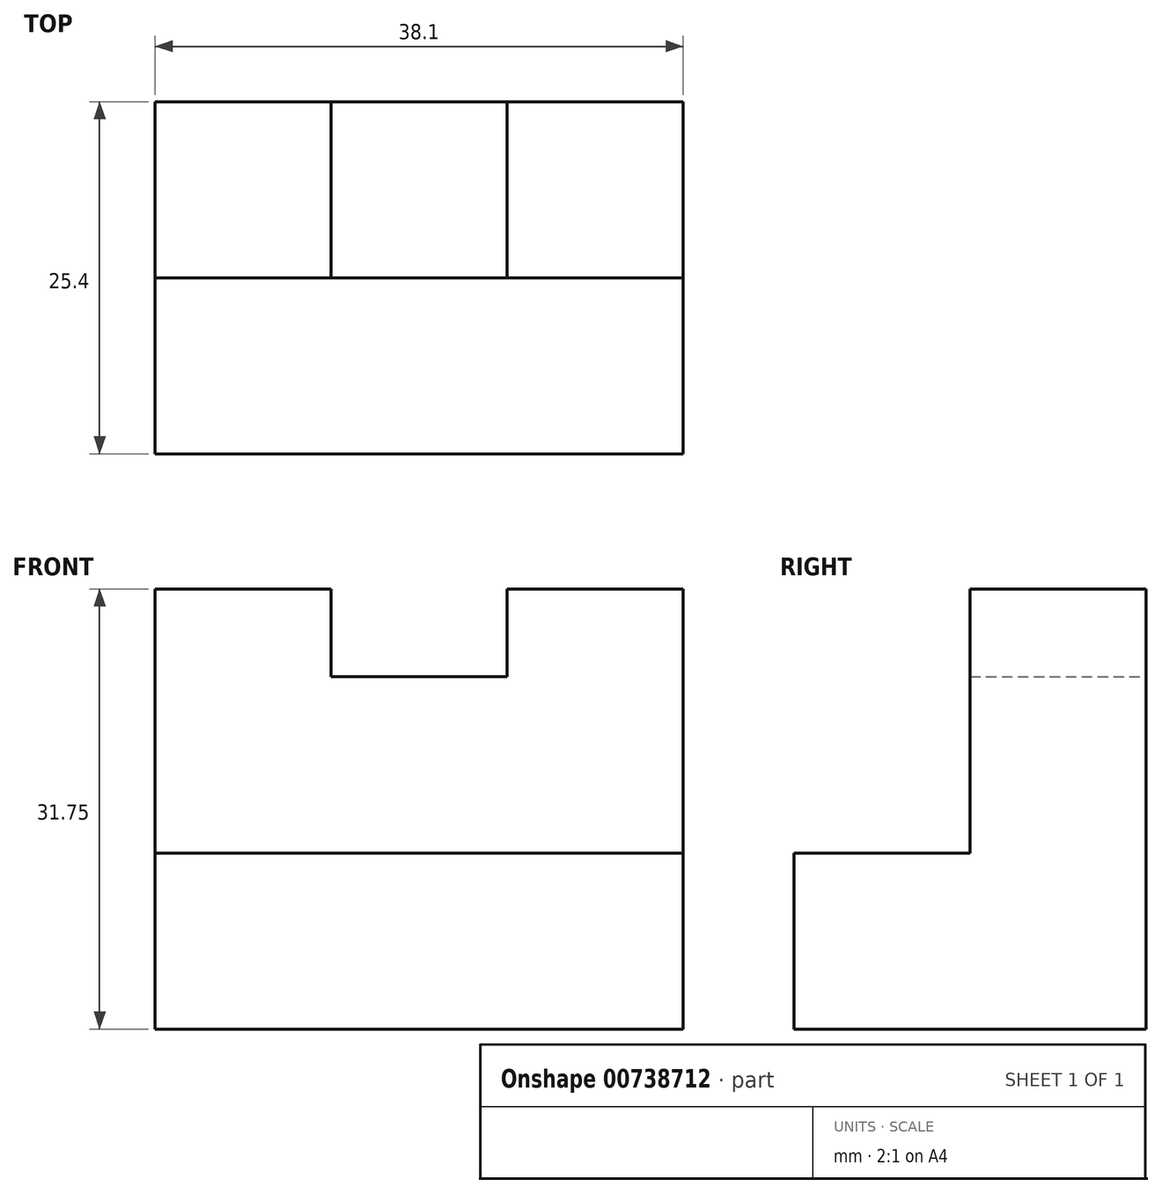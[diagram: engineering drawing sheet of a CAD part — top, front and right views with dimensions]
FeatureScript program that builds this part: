
annotation { "Feature Type Name" : "Feature", "Feature Type Description" : "" }
export const myFeature = defineFeature(function(context is Context, id is Id, definition is map)
    precondition{}
    {
        {
            var Q0;
            Q0=qCreatedBy(makeId("Right.planeOp"),FACE);
            var sketch = newSketch(context, id + "F0", { "sketchPlane" : qUnion([Q0])});
            skLineSegment(sketch, "E0", {"start": v(0, 31.75) * mm, "end": v(0, 0) * mm});
            skLineSegment(sketch, "E1", {"start": v(0, 0) * mm, "end": v(-25.4, 0) * mm});
            skLineSegment(sketch, "E2", {"start": v(-25.4, 0) * mm, "end": v(-25.4, 12.7) * mm});
            skLineSegment(sketch, "E3", {"start": v(-25.4, 12.7) * mm, "end": v(-12.7, 12.7) * mm});
            skLineSegment(sketch, "E4", {"start": v(-12.7, 12.7) * mm, "end": v(-12.7, 31.75) * mm});
            skLineSegment(sketch, "E5", {"start": v(-12.7, 31.75) * mm, "end": v(0, 31.75) * mm});
            skSolve(sketch);
        }
        {
            var Q0;
            Q0 = qSketchRegion(id + "F0", true);
            extrude(context, id + "F1", {"entities" : qUnion([Q0]), "depth" : 38.1 * mm, "offsetDistance" : 25.4 * mm});
        }
        {
            var Q0;
            Q0=qCreatedBy(makeId("Front.planeOp"),FACE);
            var sketch = newSketch(context, id + "F2", { "sketchPlane" : qUnion([Q0])});
            skLineSegment(sketch, "E6", {"start": v(12.7, 32.22) * mm, "end": v(12.7, 25.87) * mm});
            skLineSegment(sketch, "E7", {"start": v(12.7, 25.87) * mm, "end": v(25.4, 25.87) * mm});
            skLineSegment(sketch, "E8", {"start": v(25.4, 25.87) * mm, "end": v(25.4, 32.22) * mm});
            skLineSegment(sketch, "E9", {"start": v(25.4, 32.22) * mm, "end": v(12.7, 32.22) * mm});
            skSolve(sketch);
        }
        {
            var Q0;
            Q0 = qSketchRegion(id + "F2", true);
            extrude(context, id + "F3", {"entities" : qUnion([Q0]), "operationType" : NewBodyOperationType.REMOVE, "endBound" : BoundingType.THROUGH_ALL, "oppositeDirection" : true, "depth" : 25.4 * mm, "offsetDistance" : 25.4 * mm});
        }
        {
            var Q0;
            Q0=qCreatedBy(makeId("Front.planeOp"),FACE);
            var sketch = newSketch(context, id + "F4", { "sketchPlane" : qUnion([Q0])});
            skLineSegment(sketch, "E10", {"start": v(12.7, 31.77) * mm, "end": v(12.7, 25.42) * mm});
            skLineSegment(sketch, "E11", {"start": v(12.7, 25.42) * mm, "end": v(25.4, 25.42) * mm});
            skLineSegment(sketch, "E12", {"start": v(25.4, 25.42) * mm, "end": v(25.4, 31.77) * mm});
            skLineSegment(sketch, "E13", {"start": v(25.4, 31.77) * mm, "end": v(12.7, 31.77) * mm});
            skSolve(sketch);
        }
        {
            var Q0;
            Q0 = qSketchRegion(id + "F4", true);
            extrude(context, id + "F5", {"entities" : qUnion([Q0]), "operationType" : NewBodyOperationType.REMOVE, "endBound" : BoundingType.THROUGH_ALL, "oppositeDirection" : true, "depth" : 25.4 * mm, "offsetDistance" : 25.4 * mm});
        }
        {
            var Q0;
            Q0=qCreatedBy(makeId("Front.planeOp"),FACE);
            var sketch = newSketch(context, id + "F6", { "sketchPlane" : qUnion([Q0])});
            skLineSegment(sketch, "E14", {"start": v(12.7, 32.14) * mm, "end": v(12.7, 25.79) * mm});
            skLineSegment(sketch, "E15", {"start": v(12.7, 25.79) * mm, "end": v(25.4, 25.79) * mm});
            skLineSegment(sketch, "E16", {"start": v(25.4, 25.79) * mm, "end": v(25.4, 32.14) * mm});
            skLineSegment(sketch, "E17", {"start": v(25.4, 32.14) * mm, "end": v(12.7, 32.14) * mm});
            skSolve(sketch);
        }
        {
            var Q0;
            Q0 = qSketchRegion(id + "F6", true);
            extrude(context, id + "F7", {"entities" : qUnion([Q0]), "operationType" : NewBodyOperationType.REMOVE, "endBound" : BoundingType.THROUGH_ALL, "oppositeDirection" : true, "depth" : 25.4 * mm, "offsetDistance" : 25.4 * mm});
        }
        {
            var Q0;
            Q0 = qSketchRegion(id + "F4", true);
            extrude(context, id + "F8", {"entities" : qUnion([Q0]), "operationType" : NewBodyOperationType.REMOVE, "endBound" : BoundingType.THROUGH_ALL, "depth" : 25.4 * mm, "offsetDistance" : 25.4 * mm});
        }
    });
